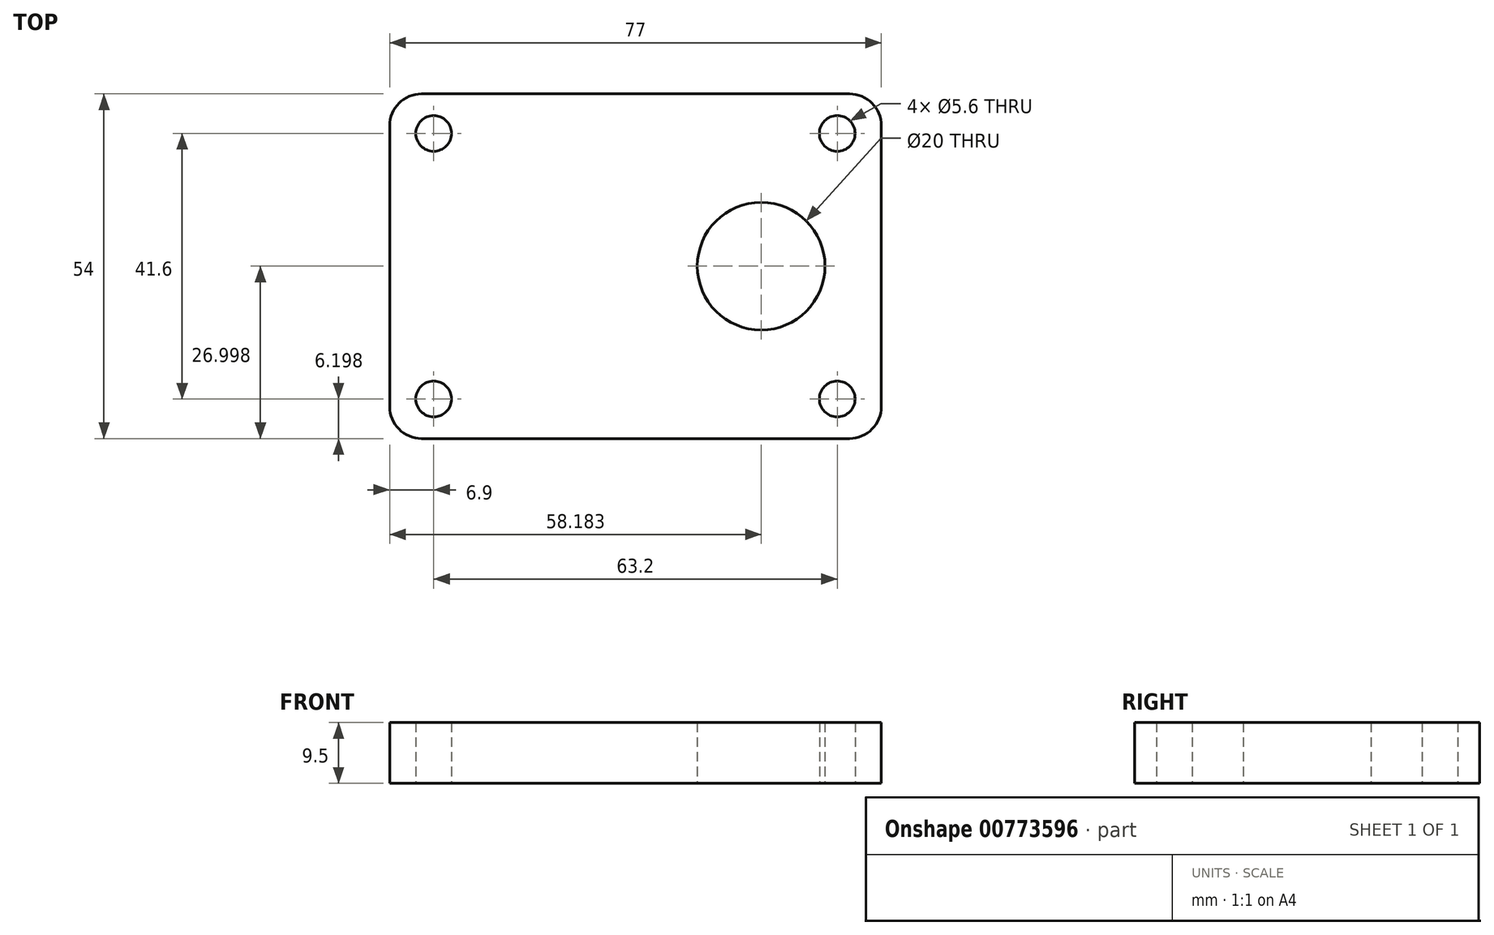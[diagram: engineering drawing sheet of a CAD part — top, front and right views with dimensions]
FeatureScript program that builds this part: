
annotation { "Feature Type Name" : "Feature", "Feature Type Description" : "" }
export const myFeature = defineFeature(function(context is Context, id is Id, definition is map)
    precondition{}
    {
        {
            var Q0;
            Q0=qCreatedBy(makeId("Top.planeOp"),FACE);
            var sketch = newSketch(context, id + "F0", { "sketchPlane" : qUnion([Q0])});
            skLineSegment(sketch, "E0.bottom", {"start": v(-36.53, 40.77) * mm, "end": v(30.47, 40.77) * mm});
            skLineSegment(sketch, "E0.top", {"start": v(-36.53, -13.23) * mm, "end": v(30.47, -13.23) * mm});
            skLineSegment(sketch, "E0.left", {"start": v(-41.53, 35.77) * mm, "end": v(-41.53, -8.23) * mm});
            skLineSegment(sketch, "E0.right", {"start": v(35.47, 35.77) * mm, "end": v(35.47, -8.23) * mm});
            skCircle(sketch, "E1", {"center": v(-34.63, 34.57) * mm, "radius": 2.8 * mm});
            skLineSegment(sketch, "E2", {"start": v(29.27, 40.77) * mm, "end": v(29.27, 34.57) * mm});
            skLineSegment(sketch, "E3", {"start": v(29.27, -7.03) * mm, "end": v(29.27, -13.23) * mm});
            skLineSegment(sketch, "E4", {"start": v(-34.63, -13.23) * mm, "end": v(-34.63, -7.03) * mm});
            skCircle(sketch, "E5", {"center": v(28.57, 34.57) * mm, "radius": 2.8 * mm});
            skCircle(sketch, "E6", {"center": v(-34.63, -7.03) * mm, "radius": 2.8 * mm});
            skCircle(sketch, "E7", {"center": v(28.57, -7.03) * mm, "radius": 2.8 * mm});
            skPoint(sketch, "E8.visualSharp", {"position": v(-41.53, 40.77) * mm});
            skArc(sketch, "E8.filletArc", {"start": v(-36.53, 40.77) * mm, "mid": v(-40.07, 39.3) * mm, "end": v(-41.53, 35.77) * mm});
            skPoint(sketch, "E9.visualSharp", {"position": v(35.47, 40.77) * mm});
            skArc(sketch, "E9.filletArc", {"start": v(35.47, 35.77) * mm, "mid": v(34, 39.3) * mm, "end": v(30.47, 40.77) * mm});
            skPoint(sketch, "E10.visualSharp", {"position": v(35.47, -13.23) * mm});
            skArc(sketch, "E10.filletArc", {"start": v(30.47, -13.23) * mm, "mid": v(34, -11.77) * mm, "end": v(35.47, -8.23) * mm});
            skPoint(sketch, "E11.visualSharp", {"position": v(-41.53, -13.23) * mm});
            skArc(sketch, "E11.filletArc", {"start": v(-41.53, -8.23) * mm, "mid": v(-40.07, -11.77) * mm, "end": v(-36.53, -13.23) * mm});
            skCircle(sketch, "E12", {"center": v(16.65, 13.77) * mm, "radius": 10 * mm});
            skPoint(sketch, "E12.centerSnap0", {"position": v(35.47, 13.77) * mm});
            skSolve(sketch);
        }
        {
            var Q0;
            Q0=qSketchRegion(id+"F0",true);
            extrude(context, id + "F1", {"entities" : qUnion([Q0]), "depth" : 9.5 * mm, "offsetDistance" : 25 * mm});
        }
    });
